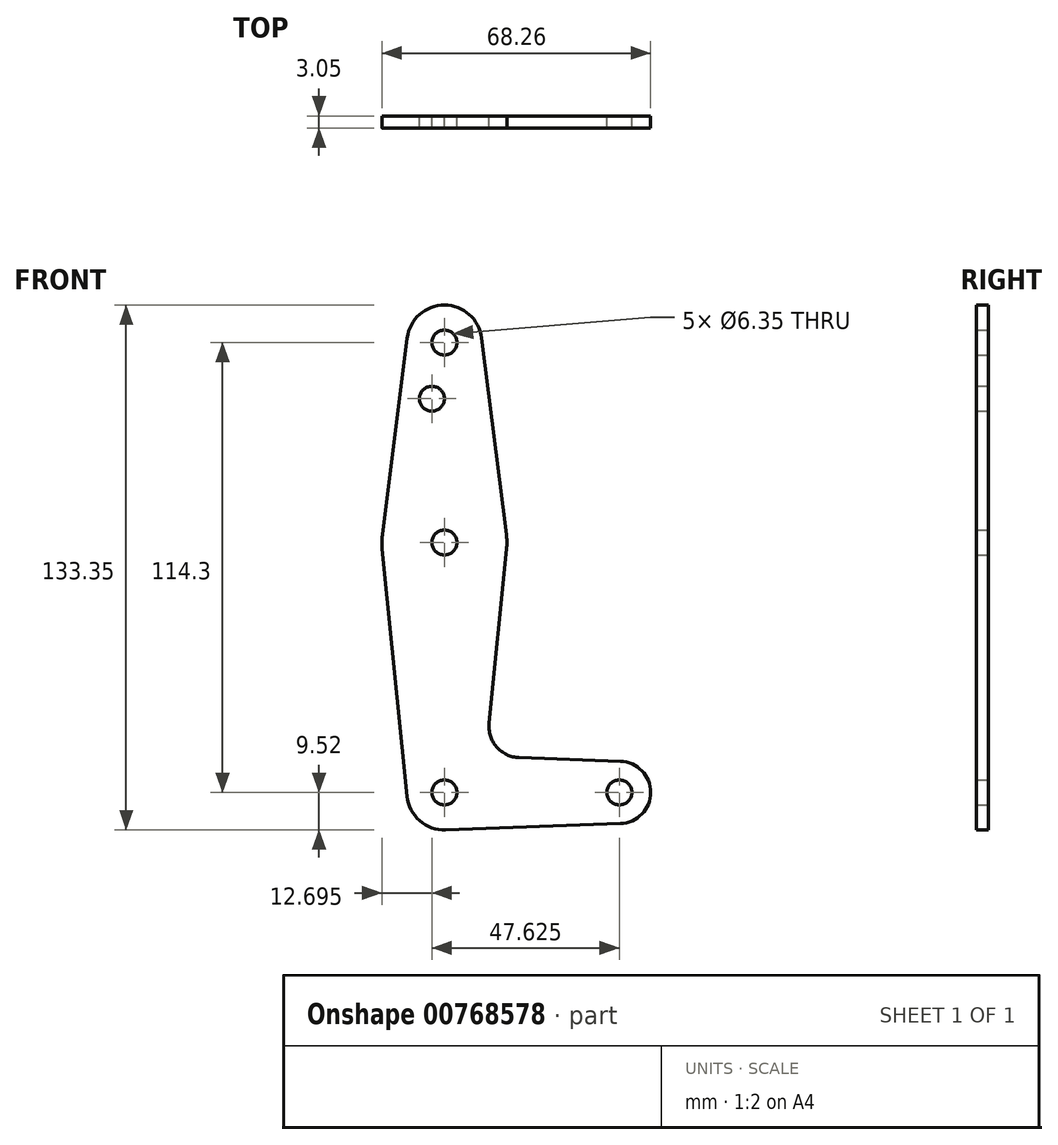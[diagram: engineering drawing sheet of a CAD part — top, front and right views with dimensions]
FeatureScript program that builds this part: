
annotation { "Feature Type Name" : "Feature", "Feature Type Description" : "" }
export const myFeature = defineFeature(function(context is Context, id is Id, definition is map)
    precondition{}
    {
        {
            var Q0;
            Q0=qCreatedBy(makeId("Front.planeOp"),FACE);
            var sketch = newSketch(context, id + "F0", { "sketchPlane" : qUnion([Q0])});
            skCircle(sketch, "E0", {"center": v(0, 0) * mm, "radius": 9.53 * mm});
            skLineSegment(sketch, "E1", {"start": v(0, 0) * mm, "end": v(0, 63.5) * mm, "construction": true});
            skCircle(sketch, "E2", {"center": v(0, 63.5) * mm, "radius": 15.88 * mm});
            skLineSegment(sketch, "E3", {"start": v(0, 63.5) * mm, "end": v(0, 114.3) * mm, "construction": true});
            skCircle(sketch, "E4", {"center": v(0, 114.3) * mm, "radius": 9.53 * mm});
            skLineSegment(sketch, "E5", {"start": v(0, 0) * mm, "end": v(44.45, 0) * mm, "construction": true});
            skCircle(sketch, "E6", {"center": v(44.45, 0) * mm, "radius": 7.94 * mm});
            skLineSegment(sketch, "E7", {"start": v(-9.45, 115.5) * mm, "end": v(-15.75, 65.48) * mm});
            skLineSegment(sketch, "E8", {"start": v(9.45, 115.5) * mm, "end": v(15.75, 65.48) * mm});
            skLineSegment(sketch, "E9", {"start": v(-15.8, 61.91) * mm, "end": v(-9.48, -0.95) * mm});
            skLineSegment(sketch, "E10", {"start": v(15.8, 61.91) * mm, "end": v(11.34, 17.6) * mm});
            skLineSegment(sketch, "E11", {"start": v(18.97, 8.85) * mm, "end": v(44.73, 7.93) * mm});
            skLineSegment(sketch, "E12", {"start": v(0.34, -9.52) * mm, "end": v(44.73, -7.93) * mm});
            skCircle(sketch, "E13", {"center": v(0, 114.3) * mm, "radius": 3.18 * mm});
            skCircle(sketch, "E14", {"center": v(0, 63.5) * mm, "radius": 3.18 * mm});
            skCircle(sketch, "E15", {"center": v(0, 0) * mm, "radius": 3.18 * mm});
            skCircle(sketch, "E16", {"center": v(44.45, 0) * mm, "radius": 3.18 * mm});
            skCircle(sketch, "E17", {"center": v(-3.18, 100.03) * mm, "radius": 3.18 * mm});
            skArc(sketch, "E18.filletArc", {"start": v(11.34, 17.6) * mm, "mid": v(13.26, 11.57) * mm, "end": v(18.97, 8.85) * mm});
            skSolve(sketch);
        }
        {
            var Q0;
            Q0 = qSketchRegion(id + "F0", true);
            extrude(context, id + "F1", {"entities" : qUnion([Q0]), "depth" : 3.05 * mm, "offsetDistance" : 25.4 * mm});
        }
    });
